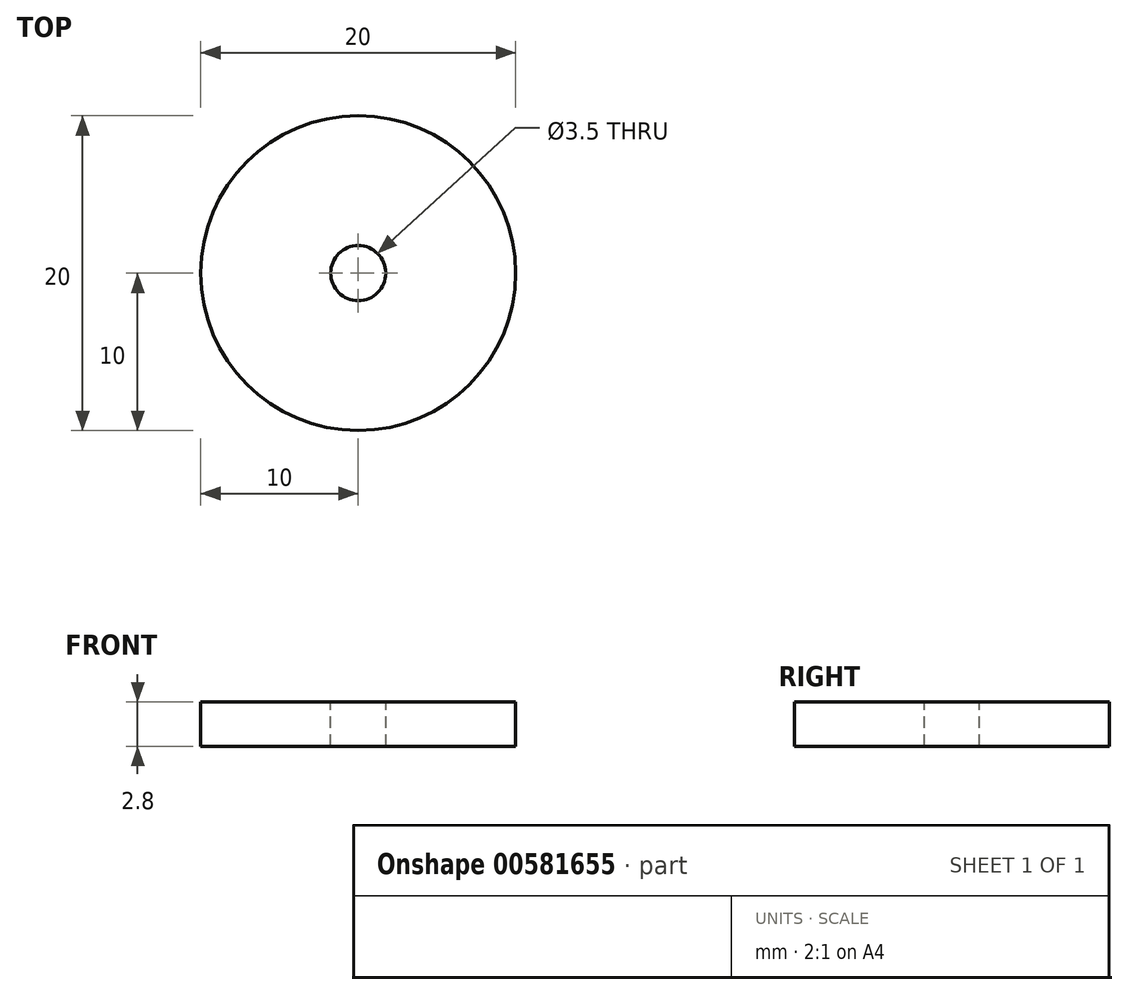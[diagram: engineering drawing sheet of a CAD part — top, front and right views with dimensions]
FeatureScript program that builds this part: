
annotation { "Feature Type Name" : "Feature", "Feature Type Description" : "" }
export const myFeature = defineFeature(function(context is Context, id is Id, definition is map)
    precondition{}
    {
        {
            var Q0;
            Q0=qCreatedBy(makeId("Top.planeOp"),FACE);
            var sketch = newSketch(context, id + "F0", { "sketchPlane" : qUnion([Q0])});
            skCircle(sketch, "E0", {"center": v(0, 0) * mm, "radius": 10 * mm});
            skSolve(sketch);
        }
        {
            var Q0;
            Q0 = qSketchRegion(id + "F0", true);
            extrude(context, id + "F1", {"entities" : qUnion([Q0]), "depth" : 2.8 * mm, "offsetDistance" : 25 * mm});
        }
        {
            var Q0;
            Q0=makeQuery(id+"F1.opExtrude","CAP_FACE",FACE,{"disambiguationData":[OSD([sQuery(id+"F0.wireOp",EDGE,"E0")])],"isStart":false});
            var sketch = newSketch(context, id + "F2", { "sketchPlane" : qUnion([Q0])});
            skCircle(sketch, "E1", {"center": v(0, 0) * mm, "radius": 1.75 * mm});
            skSolve(sketch);
        }
        {
            var Q0;
            Q0=sQuery(id+"F2.wireOp",VERTEX,"E1.center");
            var Q1;
            Q1=makeQuery(id+"F1.opExtrude","SWEPT_BODY",BODY,{"disambiguationData":[OSD([sQuery(id+"F0.wireOp",EDGE,"E0")])]});
            hole(context, id + "F3", {"style" : HoleStyle.SIMPLE, "endStyle" : HoleEndStyle.THROUGH, "holeDiameter" : 3.5 * mm, "majorDiameter" : 5 * mm, "isTappedThrough" : true, "tappedDepth" : 12 * mm, "tapClearance" : 3, "startFromSketch" : true, "locations" : qUnion([Q0]), "scope" : qUnion([Q1])});
        }
    });
